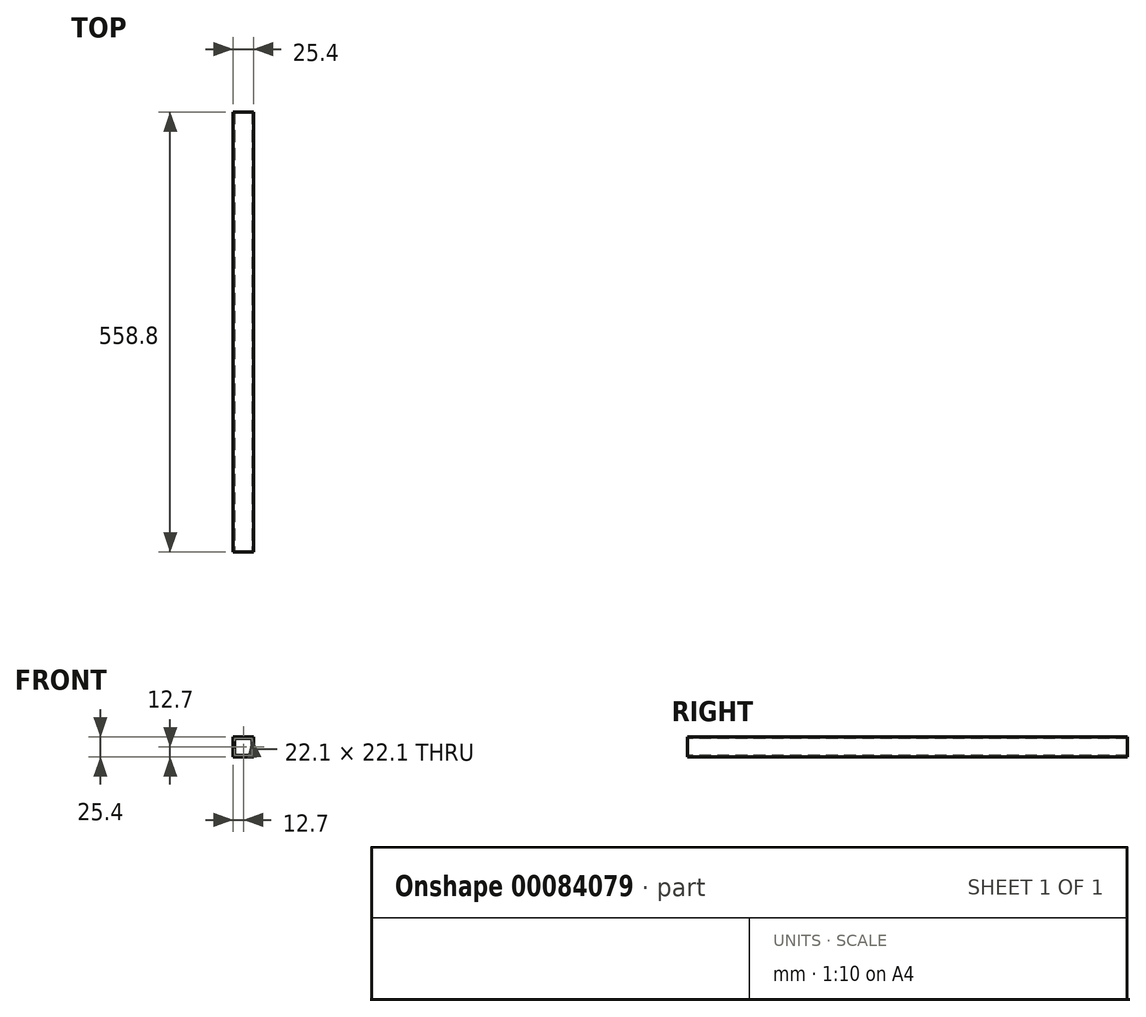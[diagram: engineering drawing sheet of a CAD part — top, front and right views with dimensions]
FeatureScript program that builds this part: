
annotation { "Feature Type Name" : "Feature", "Feature Type Description" : "" }
export const myFeature = defineFeature(function(context is Context, id is Id, definition is map)
    precondition{}
    {
        {
            var Q0;
            Q0=qCreatedBy(makeId("Front.planeOp"),FACE);
            var sketch = newSketch(context, id + "F0", { "sketchPlane" : qUnion([Q0])});
            skLineSegment(sketch, "E0.rect.bottom", {"start": v(12.7, -12.7) * mm, "end": v(-12.7, -12.7) * mm});
            skLineSegment(sketch, "E0.rect.top", {"start": v(12.7, 12.7) * mm, "end": v(-12.7, 12.7) * mm});
            skLineSegment(sketch, "E0.rect.left", {"start": v(12.7, -12.7) * mm, "end": v(12.7, 12.7) * mm});
            skLineSegment(sketch, "E0.rect.right", {"start": v(-12.7, -12.7) * mm, "end": v(-12.7, 12.7) * mm});
            skPoint(sketch, "E0.rect.middle", {"position": v(0, 0) * mm});
            skLineSegment(sketch, "E1.rect.bottom", {"start": v(11.05, -11.05) * mm, "end": v(-11.05, -11.05) * mm});
            skLineSegment(sketch, "E1.rect.top", {"start": v(11.05, 11.05) * mm, "end": v(-11.05, 11.05) * mm});
            skLineSegment(sketch, "E1.rect.left", {"start": v(11.05, -11.05) * mm, "end": v(11.05, 11.05) * mm});
            skLineSegment(sketch, "E1.rect.right", {"start": v(-11.05, -11.05) * mm, "end": v(-11.05, 11.05) * mm});
            skSolve(sketch);
        }
        {
            var Q0;
            Q0=makeQuery(id+"F0.imprint","IMPRINT",FACE,{"disambiguationData":[TD([[makeQuery(id+"F0.imprint","IMPRINT",EDGE,{"derivedFrom":sQuery(id+"F0.wireOp",EDGE,"E0.rect.bottom")}),-1.0]])]});
            extrude(context, id + "F1", {"entities" : qUnion([Q0]), "oppositeDirection" : true, "depth" : 558.8 * mm});
        }
    });
